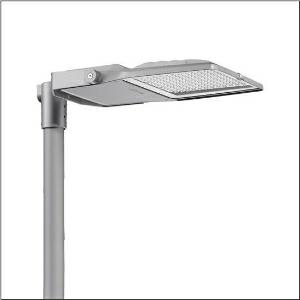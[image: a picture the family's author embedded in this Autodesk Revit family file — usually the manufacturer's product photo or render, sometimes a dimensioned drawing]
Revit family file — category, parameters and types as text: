
# Revit family: floodlight_fl_21_midi___pl64_5xa7782f4e3a_18cd
name_source: partatom
category: Lighting Fixtures
units: mm (PartAtom-declared; Revit-internal decimal feet)

## family parameters
Cut with Voids When Loaded = No
Host = Face
Light Source = No
Part Type = Normal
Room Calculation Point = No
Round Connector Dimension = Use Diameter
Shared = No

## types (1)
- --- (1 x LED, 36050 lm, 270.2 W, 4000K)
    Apparent Load = 270 VA
    CIE Flux Codes = 28 80 98 100 100
    Color Rendering = 70
    Color Temperature = 4000K
    Default Elevation = 1800 mm
    Description = Floodlight FL 21 midi, floodlight, primary light control with lens, of PMMA, primary optical cover: protective disc, of toughened safety glass, transparent, light distribution: PL64, light emission: direct distribution, installation type: surface-mounted, LED, High Power LED, rated luminous flux: 36.050lm, luminous efficacy: 133lm/W, light colour: 740, colour temperature: 4000K, control gear: ECG iQ, control: optimised constant luminous flux control (CLO 2.0), Desk-Remote (wireless, voltage-free reading and setting of iQ features in the workshop via application-optimized NFC function/RFID function), Smart-Wire, Night-Set, Temp-Guard, Auto-Match, Street-Remote, with terminal, 6-pole, mains connection: 220..240V, AC, 50/60Hz, start of lifetime: 270W, end of lifetime: 286W, reduction: 133W, luminaire housing, of diecast aluminium, powder-coated, Siteco® metallic grey (DB 702S), corrosivity category C5 according to DIN EN ISO 12944, mast bracket, of steel, galvanised, powder-coated, Siteco® metallic grey (DB 702S), protection rating (complete): IP66, insulation class (complete): insulation class II (safety insulation), certification: CE, protection symbol: D, impact resistance: IK08, permissible operating ambient temperature: -40..+40°C, permissible operating ambient temperature for outdoor applications: -40..+50°C, standard: DIN EN 12944, packaging unit: 1 piece

Light Distribution: PL64
    Height = 76 mm
    Lamp = 1 x LED
    Lamp Light Flux = 36050 lm
    Lamp Power = 270.2 W
    Lamp count = 1
    Length = 657 mm
    Luminous efficacy = 133 lm/W
    Manufacturer = Siteco
    ModVariant = No
    Model = 5XA7782F4E3A
    Number of Poles = 1
    OnlyDefault = Yes
    Power Factor = 1
    Product Name = Floodlight FL 21 midi | PL64
    Product group = floodlight | pylon top
    ProductGroupID = 6101
    Protection Class = Protection class II
    Protection Degree = IP 66
    RLX_Detail_Level = 1
    RlxData = <blob elided: 153433 chars, md5=f87c1842>
    Socket = socket
    Standby Power = 0 W
    System Light Flux = 36050 lm
    System Power = 270 W
    Type Comments = factory setting: luminous flux: 100 % | dim-lin: 254 | 620 mA
    Type Image = l_1007123.jpg
    URL = http://relux.com
    VarID = @adj_015043
    Voltage = 0 V
    Weight = 0.00 kg
    Width = 442 mm

## geometry (parser evidence)
native form markers: Blend x4, Sweep x15
no freeform markers — native parametric forms only
